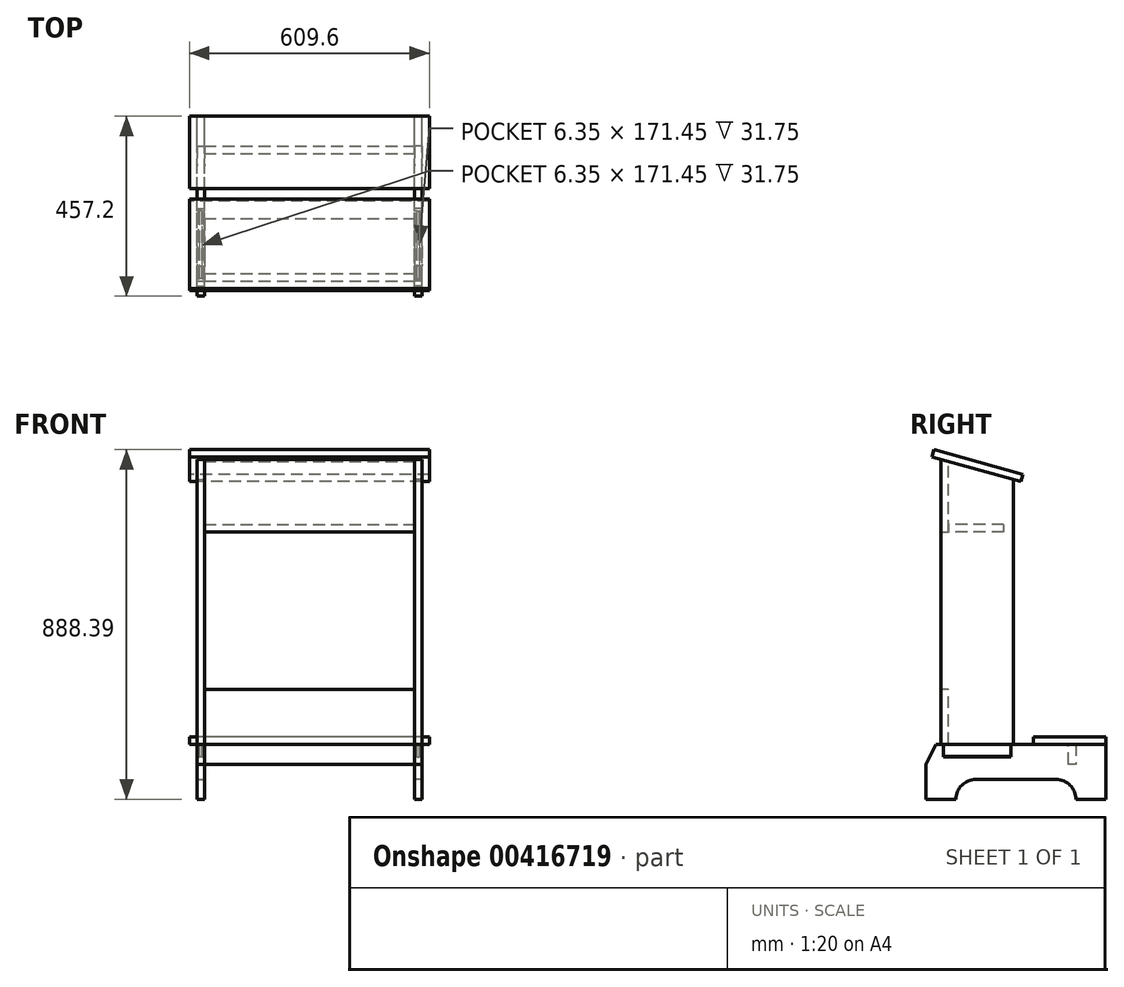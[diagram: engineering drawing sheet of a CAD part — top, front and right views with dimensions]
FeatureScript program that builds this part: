
annotation { "Feature Type Name" : "Feature", "Feature Type Description" : "" }
export const myFeature = defineFeature(function(context is Context, id is Id, definition is map)
    precondition{}
    {
        {
            var Q0;
            Q0=qCreatedBy(makeId("Right.planeOp"),FACE);
            cPlane(context, id + "F0", {"entities" : qUnion([Q0]), "cplaneType" : CPlaneType.OFFSET, "offset" : 276.22 * mm, "width" : 152.4 * mm, "height" : 152.4 * mm});
        }
        {
            var Q0;
            Q0=qCreatedBy(id+"F0.planeOp",FACE);
            var sketch = newSketch(context, id + "F1", { "sketchPlane" : qUnion([Q0])});
            skLineSegment(sketch, "E0.bottom", {"start": v(-228.6, 0) * mm, "end": v(-152.4, 0) * mm});
            skLineSegment(sketch, "E0.top", {"start": v(-203.2, 139.7) * mm, "end": v(228.6, 139.7) * mm});
            skLineSegment(sketch, "E0.left", {"start": v(-228.6, 0) * mm, "end": v(-228.6, 88.9) * mm});
            skLineSegment(sketch, "E0.right", {"start": v(228.6, 0) * mm, "end": v(228.6, 139.7) * mm});
            skPoint(sketch, "E1.endSnap0", {"position": v(0, 0) * mm});
            skArc(sketch, "E2", {"start": v(-152.4, 0) * mm, "mid": v(-137.52, 35.92) * mm, "end": v(-101.6, 50.8) * mm});
            skArc(sketch, "E3", {"start": v(152.4, 0) * mm, "mid": v(137.52, 35.92) * mm, "end": v(101.6, 50.8) * mm});
            skLineSegment(sketch, "E4", {"start": v(-101.6, 50.8) * mm, "end": v(-101.6, 50.8) * mm});
            skLineSegment(sketch, "E5", {"start": v(-101.6, 50.8) * mm, "end": v(101.6, 50.8) * mm});
            skLineSegment(sketch, "E6.trimOffspring", {"start": v(152.4, 0) * mm, "end": v(228.6, 0) * mm});
            skLineSegment(sketch, "E7", {"start": v(-228.6, 88.9) * mm, "end": v(-203.2, 139.7) * mm});
            skArc(sketch, "E8", {"start": v(-101.6, 50.8) * mm, "mid": v(-137.52, 35.92) * mm, "end": v(-152.4, 0) * mm});
            skSolve(sketch);
        }
        {
            var Q0;
            Q0 = qSketchRegion(id + "F1", true);
            extrude(context, id + "F2", {"entities" : qUnion([Q0]), "depth" : 19.05 * mm, "offsetDistance" : 25.4 * mm, "symmetric" : true});
        }
        {
            var Q0;
            Q0=qCreatedBy(id+"F0.planeOp",FACE);
            var sketch = newSketch(context, id + "F3", { "sketchPlane" : qUnion([Q0])});
            skLineSegment(sketch, "E9.bottom", {"start": v(-190.5, 139.7) * mm, "end": v(-184.15, 139.7) * mm});
            skLineSegment(sketch, "E9.left", {"start": v(-190.5, 139.7) * mm, "end": v(-190.5, 863.6) * mm});
            skLineSegment(sketch, "E9.right", {"start": v(-6.35, 139.7) * mm, "end": v(-6.35, 812.8) * mm});
            skLineSegment(sketch, "E10", {"start": v(-190.5, 863.6) * mm, "end": v(-6.35, 812.8) * mm});
            skLineSegment(sketch, "E11", {"start": v(-184.15, 139.7) * mm, "end": v(-184.15, 107.95) * mm});
            skLineSegment(sketch, "E12", {"start": v(-184.15, 107.95) * mm, "end": v(-12.7, 107.95) * mm});
            skLineSegment(sketch, "E13", {"start": v(-12.7, 107.95) * mm, "end": v(-12.7, 139.7) * mm});
            skLineSegment(sketch, "E14.trimOffspring", {"start": v(-12.7, 139.7) * mm, "end": v(-6.35, 139.7) * mm});
            skSolve(sketch);
        }
        {
            var Q0;
            Q0 = qSketchRegion(id + "F3", true);
            extrude(context, id + "F4", {"entities" : qUnion([Q0]), "depth" : 19.05 * mm, "offsetDistance" : 25.4 * mm, "symmetric" : true});
        }
        {
            var Q0;
            Q0=makeQuery(id+"F4.opExtrude","CAP_FACE",FACE,{"disambiguationData":[OSD([sQuery(id+"F3.wireOp",EDGE,"E9.bottom"),sQuery(id+"F3.wireOp",EDGE,"E9.left"),sQuery(id+"F3.wireOp",EDGE,"E9.right"),sQuery(id+"F3.wireOp",EDGE,"E10"),sQuery(id+"F3.wireOp",EDGE,"E11"),sQuery(id+"F3.wireOp",EDGE,"E12"),sQuery(id+"F3.wireOp",EDGE,"E13"),sQuery(id+"F3.wireOp",EDGE,"E14.trimOffspring")])],"isStart":false});
            var sketch = newSketch(context, id + "F5", { "sketchPlane" : qUnion([Q0])});
            skLineSegment(sketch, "E15.bottom", {"start": v(-184.15, 107.95) * mm, "end": v(-12.7, 107.95) * mm});
            skLineSegment(sketch, "E15.top", {"start": v(-184.15, 139.7) * mm, "end": v(-12.7, 139.7) * mm});
            skLineSegment(sketch, "E15.left", {"start": v(-184.15, 107.95) * mm, "end": v(-184.15, 139.7) * mm});
            skLineSegment(sketch, "E15.right", {"start": v(-12.7, 107.95) * mm, "end": v(-12.7, 139.7) * mm});
            skSolve(sketch);
        }
        {
            var Q0;
            Q0 = qSketchRegion(id + "F5", true);
            extrude(context, id + "F6", {"entities" : qUnion([Q0]), "operationType" : NewBodyOperationType.REMOVE, "oppositeDirection" : true, "depth" : 4.76 * mm, "offsetDistance" : 25.4 * mm});
        }
        {
            var Q0;
            Q0=makeQuery(id+"F4.opExtrude","CAP_FACE",FACE,{"disambiguationData":[OSD([sQuery(id+"F3.wireOp",EDGE,"E9.bottom"),sQuery(id+"F3.wireOp",EDGE,"E9.left"),sQuery(id+"F3.wireOp",EDGE,"E9.right"),sQuery(id+"F3.wireOp",EDGE,"E10"),sQuery(id+"F3.wireOp",EDGE,"E11"),sQuery(id+"F3.wireOp",EDGE,"E12"),sQuery(id+"F3.wireOp",EDGE,"E13"),sQuery(id+"F3.wireOp",EDGE,"E14.trimOffspring")])],"isStart":true});
            var sketch = newSketch(context, id + "F7", { "sketchPlane" : qUnion([Q0])});
            skLineSegment(sketch, "E16.bottom", {"start": v(12.7, 107.95) * mm, "end": v(184.15, 107.95) * mm});
            skLineSegment(sketch, "E16.top", {"start": v(12.7, 139.7) * mm, "end": v(184.15, 139.7) * mm});
            skLineSegment(sketch, "E16.left", {"start": v(12.7, 107.95) * mm, "end": v(12.7, 139.7) * mm});
            skLineSegment(sketch, "E16.right", {"start": v(184.15, 107.95) * mm, "end": v(184.15, 139.7) * mm});
            skSolve(sketch);
        }
        {
            var Q0;
            Q0 = qSketchRegion(id + "F7", true);
            extrude(context, id + "F8", {"entities" : qUnion([Q0]), "operationType" : NewBodyOperationType.REMOVE, "oppositeDirection" : true, "depth" : 4.76 * mm, "offsetDistance" : 25.4 * mm});
        }
        {
            var Q0;
            Q0=makeQuery(id+"F6.boolean.opBoolean","COPY",EDGE,{"derivedFrom":makeQuery(id+"F6.opExtrude","CAP_EDGE",EDGE,{"disambiguationData":[OSD([sQuery(id+"F5.wireOp",EDGE,"E15.bottom")])],"isStart":false})});
            var Q1;
            Q1=makeQuery(id+"F8.boolean.opBoolean","COPY",EDGE,{"derivedFrom":makeQuery(id+"F8.opExtrude","CAP_EDGE",EDGE,{"disambiguationData":[OSD([sQuery(id+"F7.wireOp",EDGE,"E16.bottom")])],"isStart":false})});
            chamfer(context, id + "F9", {"entities" : qUnion([Q0, Q1]), "width" : 1.52 * mm, "tangentPropagation" : true});
        }
        {
            var Q0;
            Q0=makeQuery(id+"F2.opExtrude","SWEPT_FACE",FACE,{"disambiguationData":[OSD([sQuery(id+"F1.wireOp",EDGE,"E0.top")])]});
            var sketch = newSketch(context, id + "F10", { "sketchPlane" : qUnion([Q0])});
            skLineSegment(sketch, "E17.bottom", {"start": v(273.05, -184.15) * mm, "end": v(279.4, -184.15) * mm});
            skLineSegment(sketch, "E17.top", {"start": v(273.05, -12.7) * mm, "end": v(279.4, -12.7) * mm});
            skLineSegment(sketch, "E17.left", {"start": v(273.05, -184.15) * mm, "end": v(273.05, -12.7) * mm});
            skLineSegment(sketch, "E17.right", {"start": v(279.4, -184.15) * mm, "end": v(279.4, -12.7) * mm});
            skSolve(sketch);
        }
        {
            var Q0;
            Q0 = qSketchRegion(id + "F10", true);
            extrude(context, id + "F11", {"entities" : qUnion([Q0]), "operationType" : NewBodyOperationType.REMOVE, "oppositeDirection" : true, "depth" : 31.75 * mm, "offsetDistance" : 25.4 * mm});
        }
        {
            var Q0;
            Q0=makeQuery(id+"F2.opExtrude","SWEPT_BODY",BODY,{"disambiguationData":[OSD([sQuery(id+"F1.wireOp",EDGE,"E0.bottom"),sQuery(id+"F1.wireOp",EDGE,"E0.top"),sQuery(id+"F1.wireOp",EDGE,"E0.left"),sQuery(id+"F1.wireOp",EDGE,"E0.right"),sQuery(id+"F1.wireOp",EDGE,"E2"),sQuery(id+"F1.wireOp",EDGE,"E3"),sQuery(id+"F1.wireOp",EDGE,"E4"),sQuery(id+"F1.wireOp",EDGE,"E5"),sQuery(id+"F1.wireOp",EDGE,"FVDVkrm0-sniB-2Jy5-Ex7j-Icef6OYxr8Z8"),sQuery(id+"F1.wireOp",EDGE,"E6.trimOffspring"),sQuery(id+"F1.wireOp",EDGE,"E7"),sQuery(id+"F1.wireOp",EDGE,"XDfoUPRw-LIe9-S4a5-1MRh-0vP5xPNhR5Hs")])]});
            var Q1;
            Q1=makeQuery(id+"F4.opExtrude","SWEPT_BODY",BODY,{"disambiguationData":[OSD([sQuery(id+"F3.wireOp",EDGE,"E9.bottom"),sQuery(id+"F3.wireOp",EDGE,"E9.left"),sQuery(id+"F3.wireOp",EDGE,"E9.right"),sQuery(id+"F3.wireOp",EDGE,"E10"),sQuery(id+"F3.wireOp",EDGE,"E11"),sQuery(id+"F3.wireOp",EDGE,"E12"),sQuery(id+"F3.wireOp",EDGE,"E13"),sQuery(id+"F3.wireOp",EDGE,"E14.trimOffspring")])]});
            var Q2;
            Q2=qCreatedBy(makeId("Right.planeOp"),FACE);
            mirror(context, id + "F12", {"entities" : qUnion([Q0, Q1]), "mirrorPlane" : qUnion([Q2])});
        }
        {
            var Q0;
            Q0=makeQuery(id+"F4.opExtrude","CAP_FACE",FACE,{"disambiguationData":[OSD([sQuery(id+"F3.wireOp",EDGE,"E9.bottom"),sQuery(id+"F3.wireOp",EDGE,"E9.left"),sQuery(id+"F3.wireOp",EDGE,"E9.right"),sQuery(id+"F3.wireOp",EDGE,"E10"),sQuery(id+"F3.wireOp",EDGE,"E11"),sQuery(id+"F3.wireOp",EDGE,"E12"),sQuery(id+"F3.wireOp",EDGE,"E13"),sQuery(id+"F3.wireOp",EDGE,"E14.trimOffspring")])],"isStart":true});
            var sketch = newSketch(context, id + "F13", { "sketchPlane" : qUnion([Q0])});
            skLineSegment(sketch, "E18", {"start": v(190.5, 863.6) * mm, "end": v(190.5, 679.45) * mm});
            skLineSegment(sketch, "E19", {"start": v(190.5, 679.45) * mm, "end": v(171.45, 679.45) * mm});
            skLineSegment(sketch, "E20", {"start": v(171.45, 679.45) * mm, "end": v(171.45, 858.34) * mm});
            skLineSegment(sketch, "E21", {"start": v(171.45, 858.34) * mm, "end": v(190.5, 863.6) * mm});
            skSolve(sketch);
        }
        {
            var Q0;
            Q0 = qSketchRegion(id + "F13", true);
            extrude(context, id + "F14", {"entities" : qUnion([Q0]), "depth" : 533.4 * mm, "offsetDistance" : 25.4 * mm});
        }
        {
            var Q0;
            Q0=makeQuery(id+"F4.opExtrude","CAP_FACE",FACE,{"disambiguationData":[OSD([sQuery(id+"F3.wireOp",EDGE,"E9.bottom"),sQuery(id+"F3.wireOp",EDGE,"E9.left"),sQuery(id+"F3.wireOp",EDGE,"E9.right"),sQuery(id+"F3.wireOp",EDGE,"E10"),sQuery(id+"F3.wireOp",EDGE,"E11"),sQuery(id+"F3.wireOp",EDGE,"E12"),sQuery(id+"F3.wireOp",EDGE,"E13"),sQuery(id+"F3.wireOp",EDGE,"E14.trimOffspring")])],"isStart":true});
            var sketch = newSketch(context, id + "F15", { "sketchPlane" : qUnion([Q0])});
            skLineSegment(sketch, "E22.bottom", {"start": v(31.75, 698.5) * mm, "end": v(171.45, 698.5) * mm});
            skLineSegment(sketch, "E22.top", {"start": v(31.75, 679.45) * mm, "end": v(171.45, 679.45) * mm});
            skLineSegment(sketch, "E22.left", {"start": v(31.75, 698.5) * mm, "end": v(31.75, 679.45) * mm});
            skLineSegment(sketch, "E22.right", {"start": v(171.45, 698.5) * mm, "end": v(171.45, 679.45) * mm});
            skSolve(sketch);
        }
        {
            var Q0;
            Q0 = qSketchRegion(id + "F15", true);
            extrude(context, id + "F16", {"entities" : qUnion([Q0]), "depth" : 533.4 * mm, "offsetDistance" : 25.4 * mm});
        }
        {
            var Q0;
            Q0=makeQuery(id+"F4.opExtrude","CAP_FACE",FACE,{"disambiguationData":[OSD([sQuery(id+"F3.wireOp",EDGE,"E9.bottom"),sQuery(id+"F3.wireOp",EDGE,"E9.left"),sQuery(id+"F3.wireOp",EDGE,"E9.right"),sQuery(id+"F3.wireOp",EDGE,"E10"),sQuery(id+"F3.wireOp",EDGE,"E11"),sQuery(id+"F3.wireOp",EDGE,"E12"),sQuery(id+"F3.wireOp",EDGE,"E13"),sQuery(id+"F3.wireOp",EDGE,"E14.trimOffspring")])],"isStart":true});
            var sketch = newSketch(context, id + "F17", { "sketchPlane" : qUnion([Q0])});
            skLineSegment(sketch, "E23.bottom", {"start": v(171.45, 139.7) * mm, "end": v(190.5, 139.7) * mm});
            skLineSegment(sketch, "E23.top", {"start": v(171.45, 279.4) * mm, "end": v(190.5, 279.4) * mm});
            skLineSegment(sketch, "E23.left", {"start": v(171.45, 139.7) * mm, "end": v(171.45, 279.4) * mm});
            skLineSegment(sketch, "E23.right", {"start": v(190.5, 139.7) * mm, "end": v(190.5, 279.4) * mm});
            skSolve(sketch);
        }
        {
            var Q0;
            Q0 = qSketchRegion(id + "F17", true);
            extrude(context, id + "F18", {"entities" : qUnion([Q0]), "depth" : 533.4 * mm, "offsetDistance" : 25.4 * mm});
        }
        {
            var Q0;
            Q0=makeQuery(id+"F2.opExtrude","CAP_FACE",FACE,{"disambiguationData":[OSD([sQuery(id+"F1.wireOp",EDGE,"E0.bottom"),sQuery(id+"F1.wireOp",EDGE,"E0.top"),sQuery(id+"F1.wireOp",EDGE,"E0.left"),sQuery(id+"F1.wireOp",EDGE,"E0.right"),sQuery(id+"F1.wireOp",EDGE,"E2"),sQuery(id+"F1.wireOp",EDGE,"E3"),sQuery(id+"F1.wireOp",EDGE,"E4"),sQuery(id+"F1.wireOp",EDGE,"E5"),sQuery(id+"F1.wireOp",EDGE,"FVDVkrm0-sniB-2Jy5-Ex7j-Icef6OYxr8Z8"),sQuery(id+"F1.wireOp",EDGE,"E6.trimOffspring"),sQuery(id+"F1.wireOp",EDGE,"E7"),sQuery(id+"F1.wireOp",EDGE,"XDfoUPRw-LIe9-S4a5-1MRh-0vP5xPNhR5Hs")])],"isStart":true});
            var sketch = newSketch(context, id + "F19", { "sketchPlane" : qUnion([Q0])});
            skLineSegment(sketch, "E24", {"start": v(-152.4, 139.7) * mm, "end": v(-152.4, 88.9) * mm});
            skLineSegment(sketch, "E25", {"start": v(-152.4, 88.9) * mm, "end": v(-133.35, 88.9) * mm});
            skLineSegment(sketch, "E26", {"start": v(-133.35, 88.9) * mm, "end": v(-133.35, 139.7) * mm});
            skLineSegment(sketch, "E27", {"start": v(-133.35, 139.7) * mm, "end": v(-152.4, 139.7) * mm});
            skSolve(sketch);
        }
        {
            var Q0;
            Q0 = qSketchRegion(id + "F19", true);
            extrude(context, id + "F20", {"entities" : qUnion([Q0]), "depth" : 533.4 * mm, "offsetDistance" : 25.4 * mm});
        }
        {
            var Q0;
            Q0=qCreatedBy(makeId("Right.planeOp"),FACE);
            var sketch = newSketch(context, id + "F21", { "sketchPlane" : qUnion([Q0])});
            skLineSegment(sketch, "E28", {"start": v(17.77, 825.9) * mm, "end": v(12.7, 807.54) * mm});
            skLineSegment(sketch, "E29", {"start": v(12.7, 807.54) * mm, "end": v(-213.8, 870.02) * mm});
            skLineSegment(sketch, "E30", {"start": v(-213.8, 870.02) * mm, "end": v(-208.72, 888.39) * mm});
            skLineSegment(sketch, "E31", {"start": v(-208.72, 888.39) * mm, "end": v(17.77, 825.9) * mm});
            skSolve(sketch);
        }
        {
            var Q0;
            Q0=makeQuery(id+"F21.imprint","IMPRINT",FACE,{"disambiguationData":[TD([[makeQuery(id+"F21.imprint","IMPRINT",EDGE,{"derivedFrom":sQuery(id+"F21.wireOp",EDGE,"E28")}),-1.0]])]});
            extrude(context, id + "F22", {"entities" : qUnion([Q0]), "depth" : 609.6 * mm, "offsetDistance" : 25.4 * mm, "symmetric" : true});
        }
        {
            var Q0;
            Q0=qCreatedBy(makeId("Right.planeOp"),FACE);
            var sketch = newSketch(context, id + "F23", { "sketchPlane" : qUnion([Q0])});
            skLineSegment(sketch, "E32", {"start": v(44.45, 139.7) * mm, "end": v(44.45, 158.75) * mm});
            skLineSegment(sketch, "E33", {"start": v(44.45, 158.75) * mm, "end": v(228.6, 158.75) * mm});
            skLineSegment(sketch, "E34", {"start": v(228.6, 158.75) * mm, "end": v(228.6, 139.7) * mm});
            skLineSegment(sketch, "E35", {"start": v(228.6, 139.7) * mm, "end": v(44.45, 139.7) * mm});
            skSolve(sketch);
        }
        {
            var Q0;
            Q0 = qSketchRegion(id + "F23", true);
            extrude(context, id + "F24", {"entities" : qUnion([Q0]), "depth" : 609.6 * mm, "offsetDistance" : 25.4 * mm, "symmetric" : true});
        }
    });
